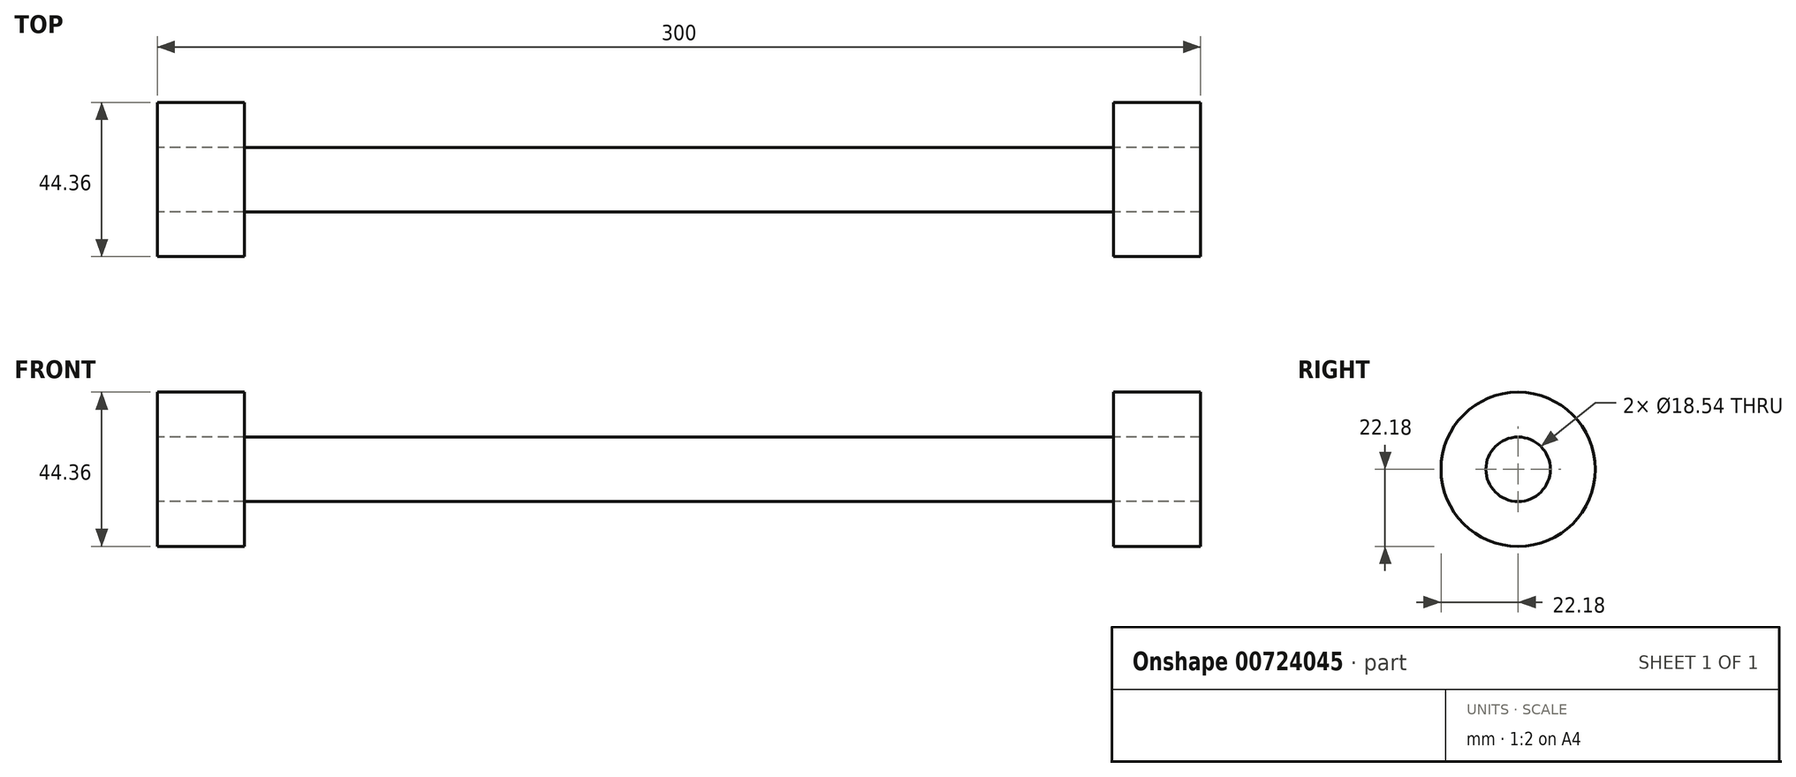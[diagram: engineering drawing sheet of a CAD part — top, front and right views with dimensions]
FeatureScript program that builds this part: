
annotation { "Feature Type Name" : "Feature", "Feature Type Description" : "" }
export const myFeature = defineFeature(function(context is Context, id is Id, definition is map)
    precondition{}
    {
        {
            var Q0;
            Q0=qCreatedBy(makeId("Right.planeOp"),FACE);
            var sketch = newSketch(context, id + "F0", { "sketchPlane" : qUnion([Q0])});
            skCircle(sketch, "E0", {"center": v(0, 0) * mm, "radius": 9.27 * mm});
            skCircle(sketch, "E1", {"center": v(0, 0) * mm, "radius": 22.18 * mm});
            skSolve(sketch);
        }
        {
            var Q0;
            Q0=makeQuery(id+"F0.imprint","IMPRINT",FACE,{"disambiguationData":[TD([[makeQuery(id+"F0.imprint","IMPRINT",EDGE,{"derivedFrom":sQuery(id+"F0.wireOp",EDGE,"E0")}),1.0]])]});
            extrude(context, id + "F1", {"entities" : qUnion([Q0]), "endBound" : BoundingType.SYMMETRIC, "depth" : 300 * mm, "offsetDistance" : 25 * mm});
        }
        {
            var Q0;
            Q0=makeQuery(id+"F0.imprint","IMPRINT",FACE,{"disambiguationData":[TD([[makeQuery(id+"F0.imprint","IMPRINT",EDGE,{"derivedFrom":sQuery(id+"F0.wireOp",EDGE,"E0")}),-1.0]])]});
            extrude(context, id + "F2", {"entities" : qUnion([Q0]), "depth" : 25 * mm, "offsetDistance" : 25 * mm});
        }
        {
            var Q0;
            Q0=makeQuery(id+"F2.opExtrude","SWEPT_BODY",BODY,{"disambiguationData":[OSD([sQuery(id+"F0.wireOp",EDGE,"E0"),sQuery(id+"F0.wireOp",EDGE,"E1")])]});
            transform(context, id + "F3", {"entities" : qUnion([Q0]), "transformType" : TransformType.TRANSLATION_3D, "dx" : 125 * mm, "dy" : 0 * mm, "dz" : 0 * mm, "makeCopy" : true});
        }
        {
            var Q0;
            Q0=makeQuery(id+"F2.opExtrude","SWEPT_BODY",BODY,{"disambiguationData":[OSD([sQuery(id+"F0.wireOp",EDGE,"E0"),sQuery(id+"F0.wireOp",EDGE,"E1")])]});
            transform(context, id + "F4", {"entities" : qUnion([Q0]), "transformType" : TransformType.TRANSLATION_3D, "dx" : -150 * mm, "dy" : 0 * mm, "dz" : 0 * mm, "makeCopy" : false});
        }
    });
